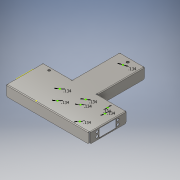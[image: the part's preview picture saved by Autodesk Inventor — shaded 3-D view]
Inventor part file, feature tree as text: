
AUTODESK INVENTOR PART (.ipt)
format: ipt  version: 2016 (Build 200138000, 138)  size: 389,632 bytes
history: native  units: in
note: dims shown in document units (in); Inventor stores cm internally (conversion verified against a paired STEP export)
features: other x14, sketch x13, sheet_metal_op x6, fillet x3
ambient origin geometry x8: Origin, YZ Plane, XZ Plane, XY Plane, X Axis, Y Axis, Z Axis, Center Point
bodies: Solid1 (feature_tree)
feature tree (36):
  sheet_metal_op  "Face1"
  sheet_metal_op  "Face2"
  sheet_metal_op  "Flange1"
  sketch  "Sketch9"  dims[d12=3.4374in]
  sketch  "Sketch18"  dims[d14=0.034in]
  sketch  "Sketch21"  dims[d16=0.068in]
  sketch  "Sketch22"  dims[d17=0.034in]
  fillet  "Fillet1"  Radius=2.3in
  fillet  "Fillet2"  Radius=8.0in
  fillet  "Fillet3"  Radius=0.034in
  sketch  "Sketch24"  dims[d19=0.017in]
  sketch  "Sketch25"  dims[d20=0.068in]
  sketch  "Sketch26"  dims[d21=0.034in d22=1.0in d23=90.0deg d24=0.034in d25=0.136in d26=0.034in d27=0.034in d40=0.034in d41=0.0in d42=0.8in d53=0.917in d55=0.034in d56=0.0in d57=0.917in d64=45.0deg d65=0.034in d66=0.0in d67=0.917in d71=1.625in d72=12.0in d73=0.0in d74=12.0in d75=0.0in d76=0.034in d77=0.0in d78=0.034in d79=0.0in d81=0.034in d82=0.0in d83=0.125in d84=0.125in d85=0.125in d86=0.231in d87=0.25in d92=0.134in d93=0.134in d94=0.134in d96=0.134in d99=0.134in d100=0.134in d101=0.134in d102=0.134in d103=0.034in d104=0.0in d105=0.034in d106=0.0in d107=0.034in d108=0.0in]
  sketch  "Sketch2"  dims[d9=3.4374in]
  other  "Plate1"
  sketch  "Sketch4"  dims[d10=2.7993in]
  other  "Plate2"
  sheet_metal_op  "Bend1"
  sketch  "Sketch5"  dims[d11=2.799in]
  other  "Plate3"
  sheet_metal_op  "Bend2"
  sheet_metal_op  "Corner1"
  sketch  "Sketch13"  dims[d13=0.034in]
  sketch  "Sketch20"  dims[d15=0.017in]
  sketch  "Sketch23"  dims[d18=0.034in]
  other  "Cut5"
  other  "Cut7"
  other  "Cut10"
  other  "Cut12"
  other  "Cut13"
  other  "Cut14"
  other  "Cut15"
  other  "Cut16"
  other  "Cut17"
  other  "Cut18"
  other  "Cut19"
